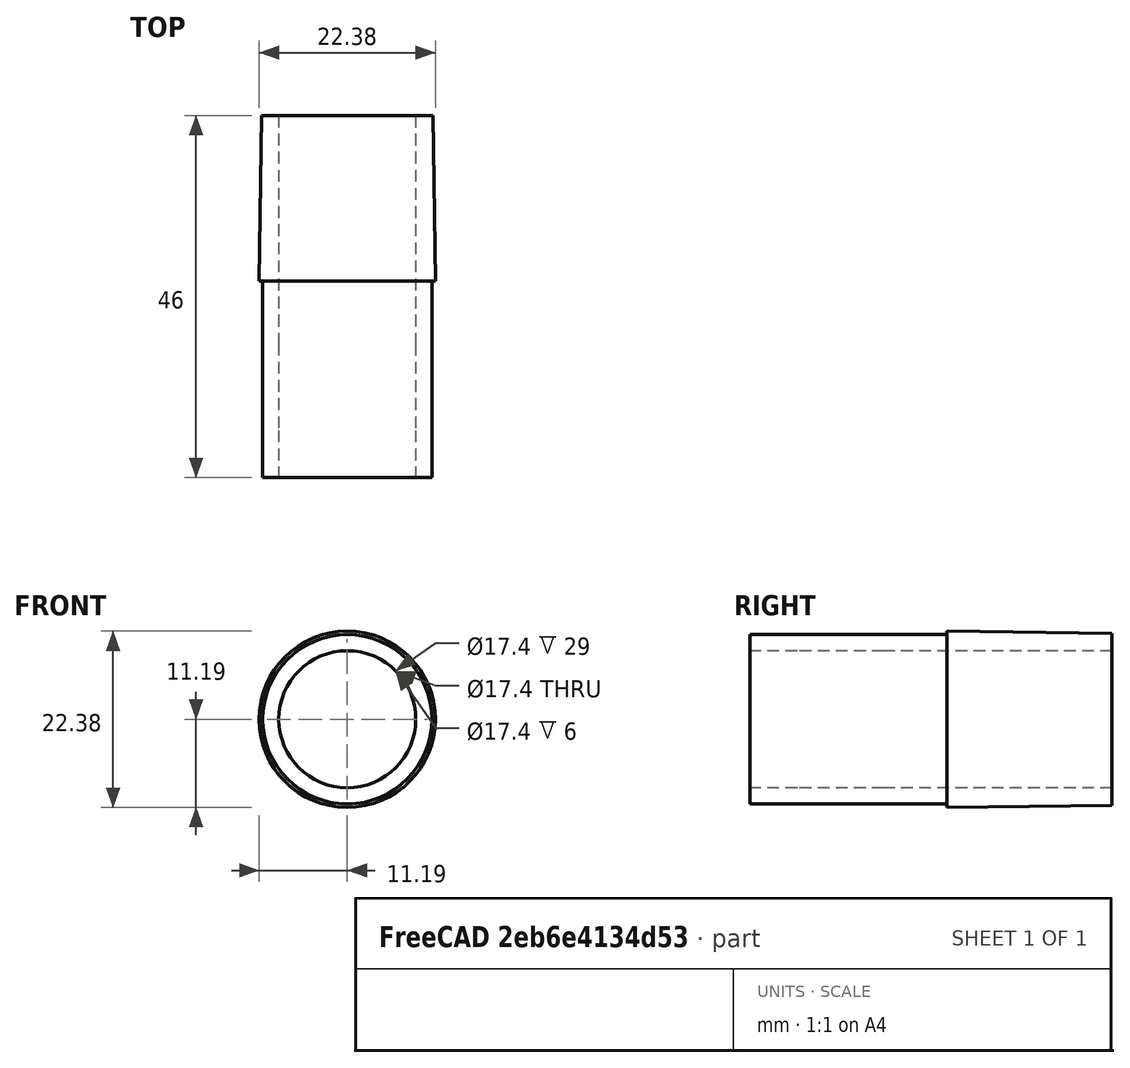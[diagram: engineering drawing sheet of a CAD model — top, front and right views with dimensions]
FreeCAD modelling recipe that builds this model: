
FCSTD DOCUMENT  (FreeCAD 0.18R4 (GitTag))
Label: BlowerOutletAdapter-V2
License: All rights reserved
LicenseURL: http://en.wikipedia.org/wiki/All_rights_reserved
objects: Part::Cylinder×3, Part::MultiFuse×2, Part::Cone×1, Part::Cut×1
note: 7 computed .brp shape members not serialized (recipe doc carries the construction recipe); baked Part::Feature solids carry a one-line shape summary decoded from their .brp

FEATURE [Part::Cone] Cone001  label="22mmTaper"
  Angle = 360
  AttacherType = Attacher::AttachEngine3D
  Height = 21
  Placement = pos=(20,65.3,13.5) rot=(0,0.707107,-0.707107;3.14159rad)
  Radius1 = 10.92
  Radius2 = 11.19
FEATURE [Part::Cylinder] Cylinder005  label="OutletExtension"
  Angle = 360
  AttacherType = Attacher::AttachEngine3D
  Height = 40
  Placement = pos=(20,65.3,13.5) rot=(1,0,0;1.5708rad)
  Radius = 8.7
FEATURE [Part::Cylinder] Cylinder007  label="HousingOutlet"
  Angle = 360
  AttacherType = Attacher::AttachEngine3D
  Height = 40
  Placement = pos=(20,59.3,13.5) rot=(1,0,0;1.5708rad)
  Radius = 10.75
FEATURE [Part::Cylinder] Cylinder003  label="BlowerOutlet"
  Angle = 360
  AttacherType = Attacher::AttachEngine3D
  Height = 40
  Placement = pos=(20,36.3,13.5) rot=(1,0,0;1.5708rad)
  Radius = 8.7
FEATURE [Part::MultiFuse] Fusion  label="Outside"
  Shapes = -> [Cone001,Cylinder007]
FEATURE [Part::MultiFuse] Fusion001  label="inside"
  Shapes = -> [Cylinder003,Cylinder005]
FEATURE [Part::Cut] Cut  label="BlowerOutletAdapter"
  Base = -> Fusion
  Tool = -> Fusion001
